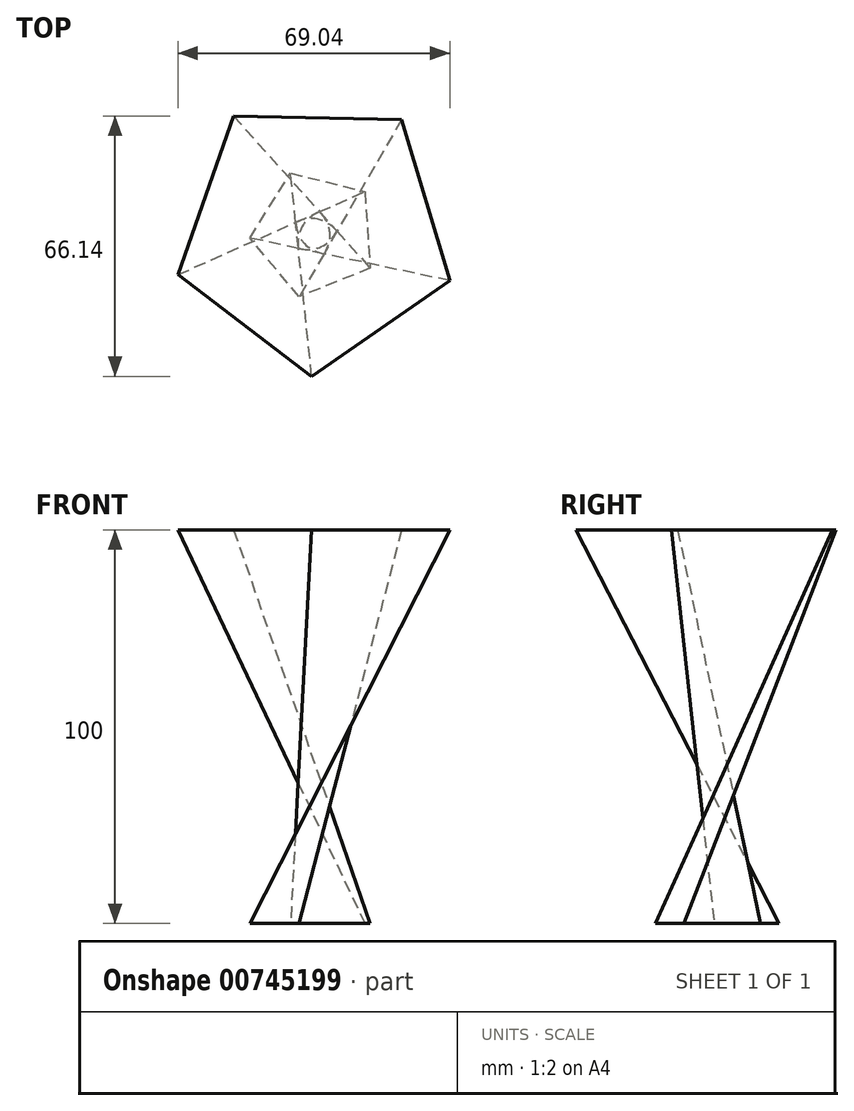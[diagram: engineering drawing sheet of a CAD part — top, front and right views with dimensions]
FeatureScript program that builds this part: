
annotation { "Feature Type Name" : "Feature", "Feature Type Description" : "" }
export const myFeature = defineFeature(function(context is Context, id is Id, definition is map)
    precondition{}
    {
        {
            var Q0;
            Q0=qCreatedBy(makeId("Top.planeOp"),FACE);
            cPlane(context, id + "F0", {"entities" : qUnion([Q0]), "cplaneType" : CPlaneType.OFFSET, "offset" : 100 * mm, "width" : 150 * mm, "height" : 150 * mm});
        }
        {
            var Q0;
            Q0=qCreatedBy(makeId("Top.planeOp"),FACE);
            var sketch = newSketch(context, id + "F1", { "sketchPlane" : qUnion([Q0])});
            skCircle(sketch, "E0.cCircle", {"center": v(0, 0) * mm, "radius": 13.4 * mm, "construction": true});
            skLineSegment(sketch, "E0.0", {"start": v(14.05, -8.78) * mm, "end": v(-4.01, -16.08) * mm});
            skLineSegment(sketch, "E0.1", {"start": v(-4.01, -16.08) * mm, "end": v(-16.53, -1.15) * mm});
            skLineSegment(sketch, "E0.2", {"start": v(-16.53, -1.15) * mm, "end": v(-6.2, 15.36) * mm});
            skLineSegment(sketch, "E0.3", {"start": v(-6.2, 15.36) * mm, "end": v(12.7, 10.65) * mm});
            skLineSegment(sketch, "E0.4", {"start": v(12.7, 10.65) * mm, "end": v(14.05, -8.78) * mm});
            skPoint(sketch, "E0.0.midPoint", {"position": v(5.02, -12.43) * mm});
            skSolve(sketch);
        }
        {
            var Q0;
            Q0=qCreatedBy(id+"F0.planeOp",FACE);
            var sketch = newSketch(context, id + "F2", { "sketchPlane" : qUnion([Q0])});
            skCircle(sketch, "E1.cCircle", {"center": v(0, 0) * mm, "radius": 29.37 * mm, "construction": true});
            skLineSegment(sketch, "E1.0", {"start": v(34.27, -11.99) * mm, "end": v(-0.8, -36.3) * mm});
            skLineSegment(sketch, "E1.1", {"start": v(-0.8, -36.3) * mm, "end": v(-34.77, -10.45) * mm});
            skLineSegment(sketch, "E1.2", {"start": v(-34.77, -10.45) * mm, "end": v(-20.68, 29.84) * mm});
            skLineSegment(sketch, "E1.3", {"start": v(-20.68, 29.84) * mm, "end": v(21.99, 28.89) * mm});
            skLineSegment(sketch, "E1.4", {"start": v(21.99, 28.89) * mm, "end": v(34.27, -11.99) * mm});
            skPoint(sketch, "E1.0.midPoint", {"position": v(16.73, -24.14) * mm});
            skSolve(sketch);
        }
        {
            var Q0;
            Q0=makeQuery(id+"F2.imprint","IMPRINT",FACE,{"disambiguationData":[TD([[makeQuery(id+"F2.imprint","IMPRINT",EDGE,{"derivedFrom":sQuery(id+"F2.wireOp",EDGE,"E1.0")}),-1.0]])]});
            var Q1;
            Q1=makeQuery(id+"F1.imprint","IMPRINT",FACE,{"disambiguationData":[TD([[makeQuery(id+"F1.imprint","IMPRINT",EDGE,{"derivedFrom":sQuery(id+"F1.wireOp",EDGE,"E0.0")}),-1.0]])]});
            var Q2;
            Q2=sQuery(id+"F2.wireOp",VERTEX,"E1.4.start");
            var Q3;
            Q3=sQuery(id+"F1.wireOp",VERTEX,"E0.1.start");
            loft(context, id + "F3", {"sheetProfilesArray" : [{ "sheetProfileEntities" : qUnion([Q0]) }, { "sheetProfileEntities" : qUnion([Q1]) }], "matchConnections" : true, "connections" : [{ "connectionEntities" : qUnion([Q2, Q3]), "connectionEdgeQueries" : qUnion([]), "connectionEdgeParameters" : [] }]});
        }
    });
